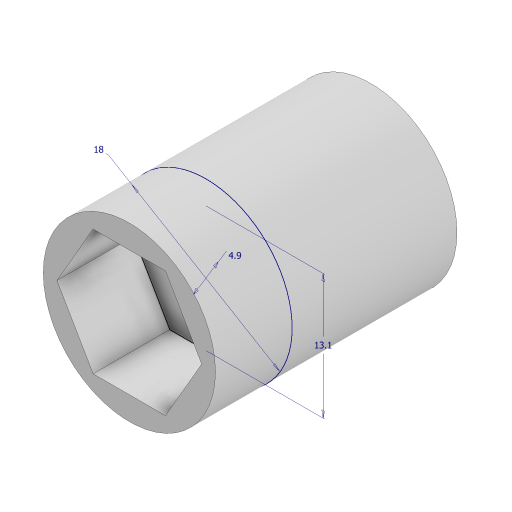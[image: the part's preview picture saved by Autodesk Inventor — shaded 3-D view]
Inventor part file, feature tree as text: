
AUTODESK INVENTOR PART (.ipt)
format: ipt  version: 2023 (Build 270158000, 158)  size: 130,048 bytes
history: native  units: mm
features: extrude x2, sketch x1
ambient origin geometry x8: Origin, YZ Plane, XZ Plane, XY Plane, X Axis, Y Axis, Z Axis, Center Point
bodies: Solid1 (feature_tree)
feature tree (3):
  sketch  "Sketch1"  dims[d0=13.1mm d1=18.0mm d2=4.9mm d3=8.0mm d4=0.0mm d5=17.25mm d6=0.0mm]
  extrude  "Extrusion1"  Depth=17.25mm
  extrude  "Extrusion2"  Depth=17.25mm
